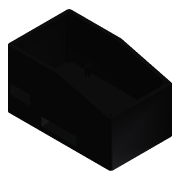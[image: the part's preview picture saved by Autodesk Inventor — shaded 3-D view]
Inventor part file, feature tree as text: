
AUTODESK INVENTOR PART (.ipt)
format: ipt  version: 2013 (Build 170138000, 138)  size: 258,048 bytes
history: native  units: in
note: dims shown in document units (in); Inventor stores cm internally (conversion verified against a paired STEP export)
features: extrude x10, sketch x10, fillet x4, hole x1, plane x1
ambient origin geometry x8: Origin, YZ Plane, XZ Plane, XY Plane, X Axis, Y Axis, Z Axis, Center Point
bodies: Solid1 (feature_tree)
feature tree (26):
  extrude  "Extrusion1"  Depth=0.125in
  extrude  "Extrusion4"  Depth=3.0in
  extrude  "Extrusion6"  Depth=0.125in
  hole  "Hole1"  [1 undecoded]
  fillet  "Fillet1"  Radius=2.0in
  fillet  "Fillet2"  Radius=0.24in
  extrude  "Extrusion9"  Depth=1.32in
  extrude  "Extrusion12"  Depth=0.015in
  fillet  "Fillet5"  Radius=0.025in
  extrude  "Extrusion13"  Depth=0.1in
  fillet  "Fillet6"  Radius=0.1in
  extrude  "Extrusion15"  Depth=0.215in
  extrude  "Extrusion23"  Depth=0.125in
  extrude  "Extrusion24"  Depth=0.125in
  plane  "Work Plane1"
  extrude  "Extrusion25"  Depth=0.125in
  sketch  "Sketch1"  dims[d0=0.1in d1=0.0in d8=0.125in]
  sketch  "Sketch5"  dims[d9=1.8in d11=3.0in]
  sketch  "Sketch6"  dims[d12=0.125in d13=0.125in]
  sketch  "Sketch8"  dims[d14=0.125in d15=1.37in d16=2.0in d17=0.24in d18=0.0in]
  sketch  "Sketch13"  dims[d21=1.96in d22=1.32in]
  sketch  "Sketch14"  dims[d23=0.25in d24=0.0in d25=0.015in d27=0.025in]
  sketch  "Sketch16"  dims[d28=0.1in d29=0.1in d30=0.1in]
  sketch  "Sketch18"  dims[d31=0.1in d32=0.215in]
  sketch  "Sketch23"  dims[d34=0.25in]
  sketch  "Sketch26"  dims[d37=0.063in d38=0.25in d39=0.375in d40=0.25in d41=0.5635in d42=0.25in d43=0.8108in d44=0.125in d45=0.125in d46=0.125in d47=0.125in d55=0.0625in d56=0.0625in d59=1.2in d60=0.0in d77=0.5709in d79=0.2835in d80=0.1in d81=0.0in d84=0.0625in d85=0.375in d86=3.0in d87=0.0in d88=0.0625in d97=1.0in d98=1.0in d99=0.125in d100=1.0in d101=0.0in d103=0.25in d110=1.5in d114=0.1in d133=2.6875in d134=0.0in d135=0.375in d136=0.1in d137=0.0625in d138=0.0625in d139=0.25in d140=0.0in d141=0.0625in d142=0.0625in d143=0.0625in d144=0.25in d145=0.0in]
note: 1 required parameter value undecoded (feature->parameter linkage not recoverable at this tier; creation-order binding heuristic only, values carry confidence <= 0.55)
